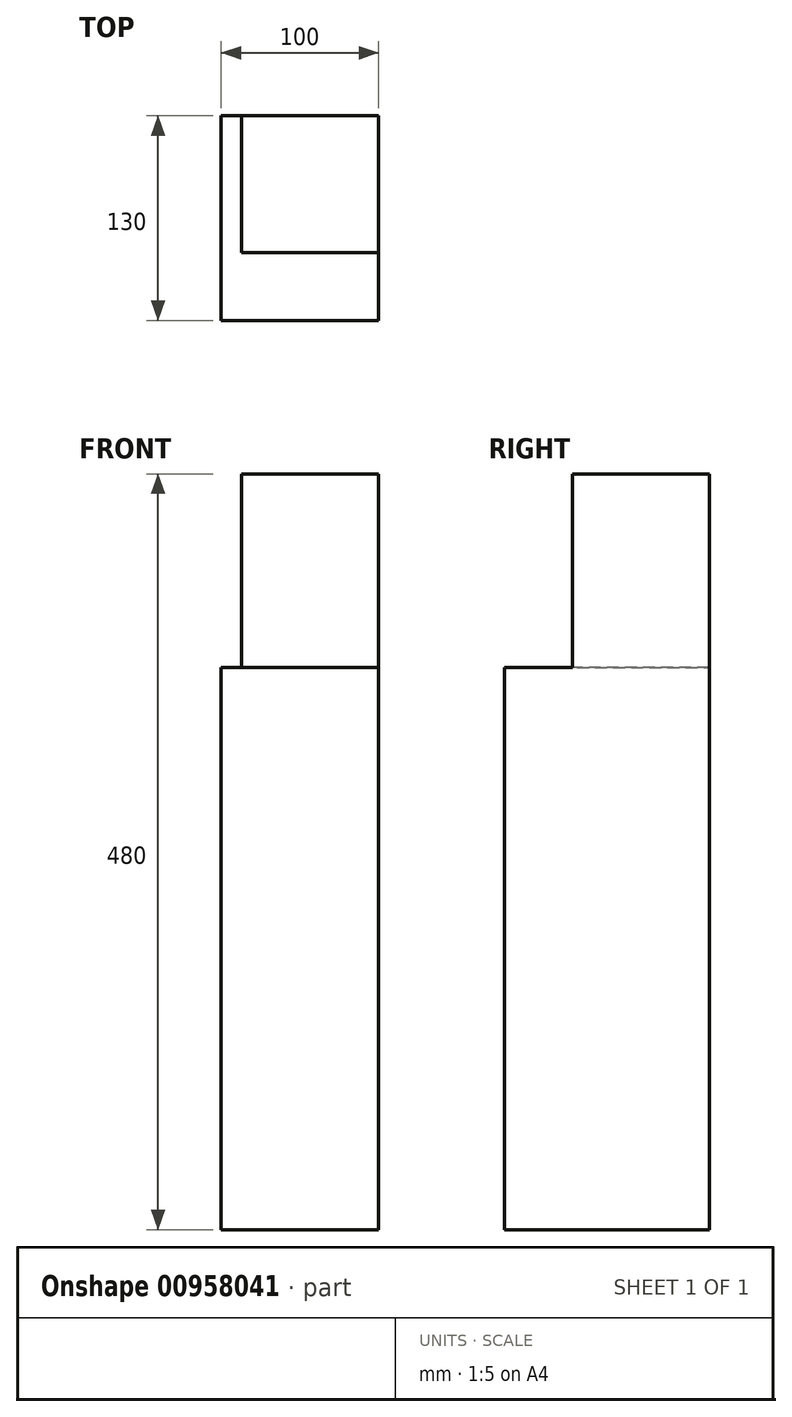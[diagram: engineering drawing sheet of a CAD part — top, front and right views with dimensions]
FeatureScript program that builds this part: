
annotation { "Feature Type Name" : "Feature", "Feature Type Description" : "" }
export const myFeature = defineFeature(function(context is Context, id is Id, definition is map)
    precondition{}
    {
        {
            var Q0;
            Q0=qCreatedBy(makeId("Top.planeOp"),FACE);
            var sketch = newSketch(context, id + "F0", { "sketchPlane" : qUnion([Q0])});
            skLineSegment(sketch, "E0.bottom", {"start": v(50, -65) * mm, "end": v(-50, -65) * mm});
            skLineSegment(sketch, "E0.top", {"start": v(50, 65) * mm, "end": v(-50, 65) * mm});
            skLineSegment(sketch, "E0.left", {"start": v(50, -65) * mm, "end": v(50, 65) * mm});
            skLineSegment(sketch, "E0.right", {"start": v(-50, -65) * mm, "end": v(-50, 65) * mm});
            skPoint(sketch, "E0.middle", {"position": v(0, 0) * mm});
            skSolve(sketch);
        }
        {
            var Q0;
            Q0=makeQuery(id+"F0.imprint","IMPRINT",FACE,{"disambiguationData":[TD([[makeQuery(id+"F0.imprint","IMPRINT",EDGE,{"derivedFrom":sQuery(id+"F0.wireOp",EDGE,"E0.bottom")}),-1.0]])]});
            extrude(context, id + "F1", {"entities" : qUnion([Q0]), "depth" : 480 * mm, "offsetDistance" : 25 * mm});
        }
        {
            var Q0;
            Q0=makeQuery(id+"F1.opExtrude","CAP_FACE",FACE,{"disambiguationData":[OSD([sQuery(id+"F0.wireOp",EDGE,"E0.bottom"),sQuery(id+"F0.wireOp",EDGE,"E0.top"),sQuery(id+"F0.wireOp",EDGE,"E0.left"),sQuery(id+"F0.wireOp",EDGE,"E0.right")])],"isStart":false});
            var sketch = newSketch(context, id + "F2", { "sketchPlane" : qUnion([Q0])});
            skLineSegment(sketch, "E1.bottom", {"start": v(-50, -65) * mm, "end": v(50, -65) * mm});
            skLineSegment(sketch, "E1.top", {"start": v(-50, -22) * mm, "end": v(50, -22) * mm});
            skLineSegment(sketch, "E1.left", {"start": v(-50, -65) * mm, "end": v(-50, -22) * mm});
            skLineSegment(sketch, "E1.right", {"start": v(50, -65) * mm, "end": v(50, -22) * mm});
            skLineSegment(sketch, "E2.bottom", {"start": v(-50, 65) * mm, "end": v(-37, 65) * mm});
            skLineSegment(sketch, "E2.top", {"start": v(-50, -65) * mm, "end": v(-37, -65) * mm});
            skLineSegment(sketch, "E2.left", {"start": v(-50, 65) * mm, "end": v(-50, -65) * mm});
            skLineSegment(sketch, "E2.right", {"start": v(-37, 65) * mm, "end": v(-37, -65) * mm});
            skSolve(sketch);
        }
        {
            var Q0;
            {var subQ5=sQuery(id+"F2.wireOp",EDGE,"E2.bottom");Q0=makeQuery(id+"F2.imprint","IMPRINT",FACE,{"disambiguationData":[TD([[makeQuery(id+"F2.imprint","IMPRINT",EDGE,{"derivedFrom":subQ5}),1.0]])]});}
            var Q1;
            {var subQ5=sQuery(id+"F2.wireOp",EDGE,"E2.top");Q1=makeQuery(id+"F2.imprint","IMPRINT",FACE,{"disambiguationData":[TD([[makeQuery(id+"F2.imprint","IMPRINT",EDGE,{"derivedFrom":subQ5}),-1.0]])]});}
            var Q2;
            {var subQ0=sQuery(id+"F2.wireOp",EDGE,"E1.bottom");Q2=makeQuery(id+"F2.imprint","IMPRINT",FACE,{"disambiguationData":[TD([[makeQuery(id+"F2.imprint","IMPRINT",EDGE,{"derivedFrom":subQ0}),-1.0]])]});}
            extrude(context, id + "F3", {"entities" : qUnion([Q0, Q1, Q2]), "operationType" : NewBodyOperationType.REMOVE, "oppositeDirection" : true, "depth" : 123 * mm, "offsetDistance" : 25 * mm});
        }
    });
